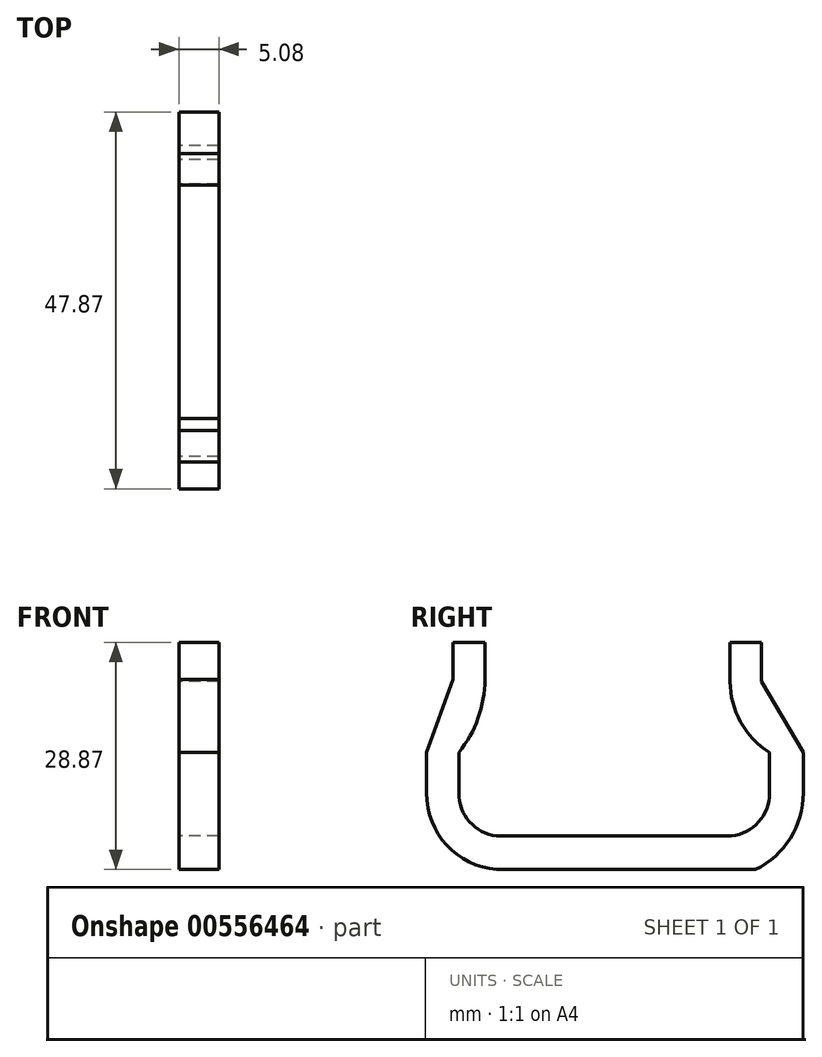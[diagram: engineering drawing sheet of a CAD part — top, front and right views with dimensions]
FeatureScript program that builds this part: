
annotation { "Feature Type Name" : "Feature", "Feature Type Description" : "" }
export const myFeature = defineFeature(function(context is Context, id is Id, definition is map)
    precondition{}
    {
        {
            var Q0;
            Q0=qCreatedBy(makeId("Right.planeOp"),FACE);
            var sketch = newSketch(context, id + "F0", { "sketchPlane" : qUnion([Q0])});
            skLineSegment(sketch, "E0", {"start": v(-20.15, -11.68) * mm, "end": v(-20.15, -16.38) * mm});
            skLineSegment(sketch, "E1", {"start": v(-16.12, -11.68) * mm, "end": v(-16.12, -16.38) * mm});
            skArc(sketch, "E2", {"start": v(-19.43, -25.68) * mm, "mid": v(-16.97, -21.32) * mm, "end": v(-16.12, -16.38) * mm});
            skLineSegment(sketch, "E3", {"start": v(-20.15, -16.38) * mm, "end": v(-23.53, -25.66) * mm});
            skLineSegment(sketch, "E4", {"start": v(-19.43, -25.68) * mm, "end": v(-19.43, -30.84) * mm});
            skLineSegment(sketch, "E5", {"start": v(-23.53, -25.66) * mm, "end": v(-23.53, -30.84) * mm});
            skArc(sketch, "E6", {"start": v(-23.53, -30.84) * mm, "mid": v(-20.97, -37.43) * mm, "end": v(-14.62, -40.55) * mm});
            skArc(sketch, "E7", {"start": v(-19.43, -30.84) * mm, "mid": v(-18.05, -34.47) * mm, "end": v(-14.62, -36.3) * mm});
            skLineSegment(sketch, "E8", {"start": v(15.03, -11.68) * mm, "end": v(15.03, -16.65) * mm});
            skLineSegment(sketch, "E9", {"start": v(19.03, -11.68) * mm, "end": v(19.03, -16.65) * mm});
            skArc(sketch, "E10", {"start": v(15.03, -16.65) * mm, "mid": v(16.37, -21.82) * mm, "end": v(20.06, -25.68) * mm});
            skLineSegment(sketch, "E11", {"start": v(19.03, -16.65) * mm, "end": v(24.34, -25.68) * mm});
            skLineSegment(sketch, "E12", {"start": v(20.06, -25.68) * mm, "end": v(20.06, -30.84) * mm});
            skLineSegment(sketch, "E13", {"start": v(24.34, -25.68) * mm, "end": v(24.34, -30.84) * mm});
            skArc(sketch, "E14", {"start": v(18.26, -40.55) * mm, "mid": v(22.7, -36.57) * mm, "end": v(24.34, -30.84) * mm});
            skArc(sketch, "E15", {"start": v(15.18, -36.3) * mm, "mid": v(18.66, -34.5) * mm, "end": v(20.06, -30.84) * mm});
            skLineSegment(sketch, "E16", {"start": v(-14.62, -36.3) * mm, "end": v(15.18, -36.3) * mm});
            skLineSegment(sketch, "E17", {"start": v(-14.62, -40.55) * mm, "end": v(18.26, -40.55) * mm});
            skLineSegment(sketch, "E18", {"start": v(-20.15, -11.68) * mm, "end": v(-16.12, -11.68) * mm});
            skLineSegment(sketch, "E19", {"start": v(15.03, -11.68) * mm, "end": v(19.03, -11.68) * mm});
            skSolve(sketch);
        }
        {
            var Q0;
            Q0 = qSketchRegion(id + "F0", true);
            extrude(context, id + "F1", {"entities" : qUnion([Q0]), "endBound" : BoundingType.SYMMETRIC, "depth" : 5.08 * mm, "offsetDistance" : 25.4 * mm});
        }
    });
